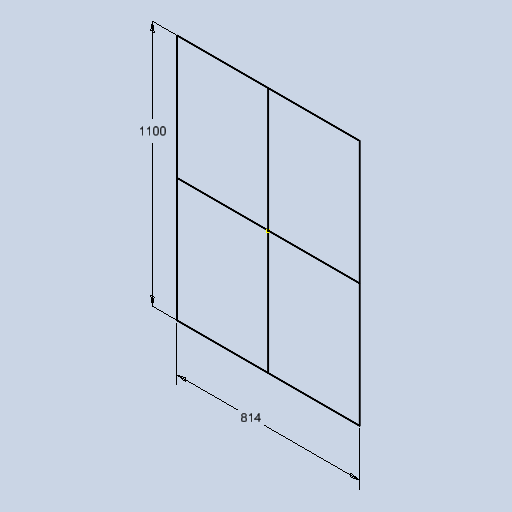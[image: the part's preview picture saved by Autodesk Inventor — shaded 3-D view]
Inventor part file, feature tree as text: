
AUTODESK INVENTOR PART (.ipt)
format: ipt  version: 2025 (Build 290162010, 162A)  size: 128,000 bytes
history: native  units: mm
features: sketch x1
ambient origin geometry x8: Origin, YZ Plane, XZ Plane, XY Plane, X Axis, Y Axis, Z Axis, Center Point
feature tree (1):
  sketch  "Sketch1"  dims[d0=1100.0mm d1=814.0mm]
